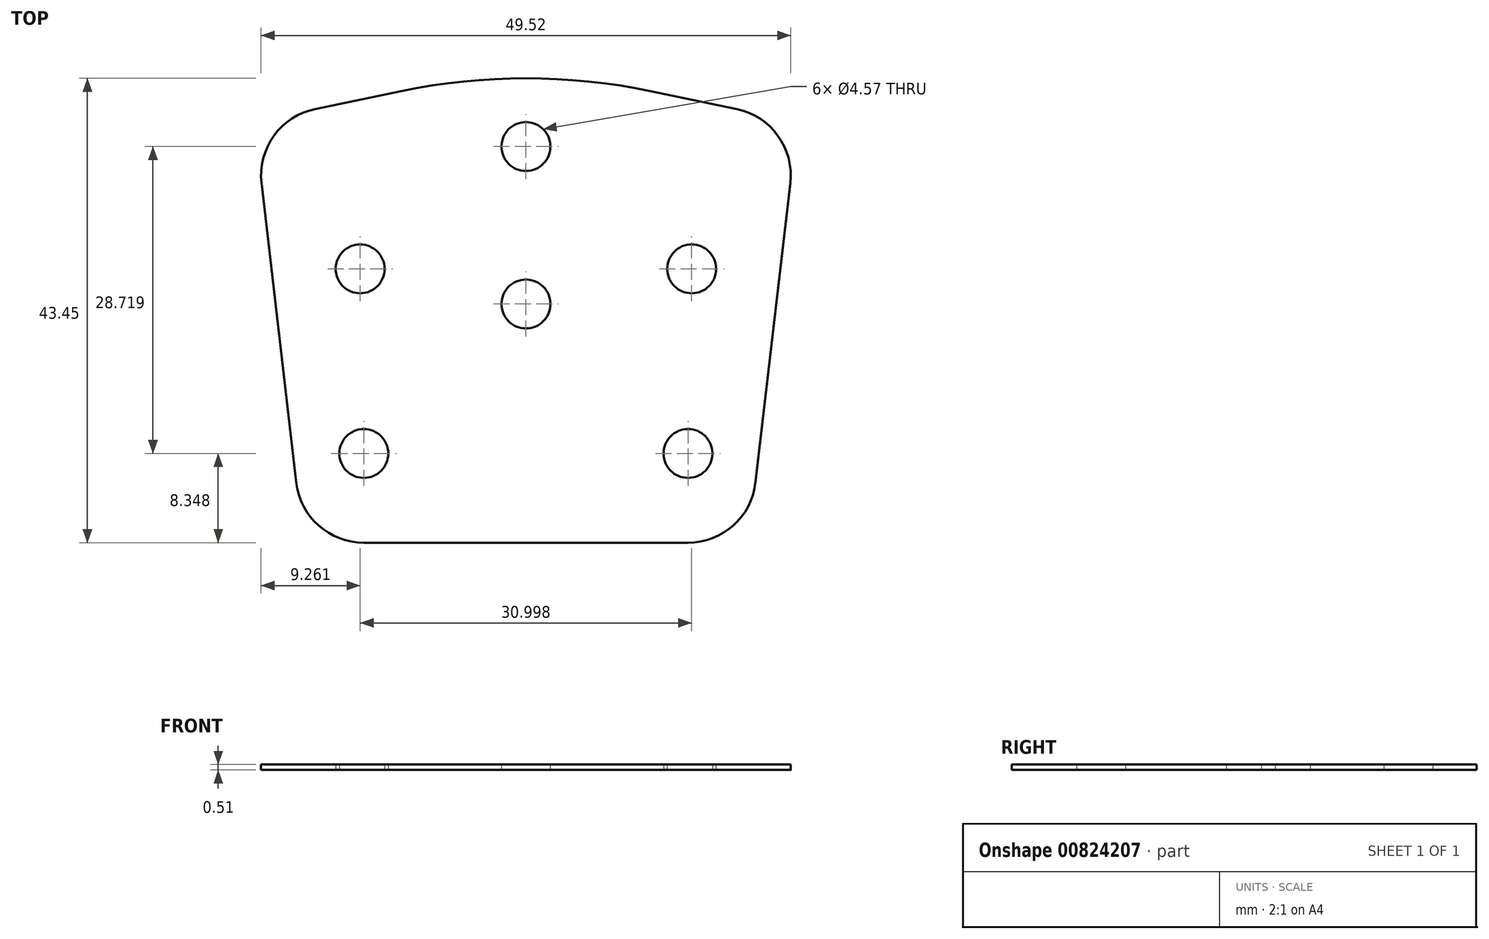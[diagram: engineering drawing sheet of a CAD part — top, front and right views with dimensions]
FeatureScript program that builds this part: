
annotation { "Feature Type Name" : "Feature", "Feature Type Description" : "" }
export const myFeature = defineFeature(function(context is Context, id is Id, definition is map)
    precondition{}
    {
        {
            var Q0;
            Q0=qCreatedBy(makeId("Top.planeOp"),FACE);
            var sketch = newSketch(context, id + "F0", { "sketchPlane" : qUnion([Q0])});
            skLineSegment(sketch, "E0", {"start": v(0, 0) * mm, "end": v(15.16, 0) * mm});
            skLineSegment(sketch, "E1", {"start": v(21.46, 5.62) * mm, "end": v(24.72, 33.62) * mm});
            skLineSegment(sketch, "E2", {"start": v(19.7, 40.57) * mm, "end": v(11.63, 42.25) * mm});
            skPoint(sketch, "E3.visualSharp", {"position": v(25.4, 39.4) * mm});
            skArc(sketch, "E3.filletArc", {"start": v(24.72, 33.62) * mm, "mid": v(23.56, 38.07) * mm, "end": v(19.7, 40.57) * mm});
            skPoint(sketch, "E4.visualSharp", {"position": v(20.81, 0) * mm});
            skArc(sketch, "E4.filletArc", {"start": v(15.16, 0) * mm, "mid": v(19.38, 1.6) * mm, "end": v(21.46, 5.62) * mm});
            skLineSegment(sketch, "E5", {"start": v(0, 44.67) * mm, "end": v(0, 0) * mm, "construction": true});
            skLineSegment(sketch, "E6.MirrorCS", {"start": v(-21.46, 5.62) * mm, "end": v(-24.72, 33.62) * mm});
            skLineSegment(sketch, "E7.MirrorCS", {"start": v(-19.7, 40.57) * mm, "end": v(-11.63, 42.25) * mm});
            skPoint(sketch, "E8.MirrorP", {"position": v(-25.4, 39.4) * mm});
            skPoint(sketch, "E9.MirrorP", {"position": v(-20.81, 0) * mm});
            skArc(sketch, "E10.MirrorCS", {"start": v(-15.16, 0) * mm, "mid": v(-19.38, 1.6) * mm, "end": v(-21.46, 5.62) * mm});
            skLineSegment(sketch, "E11.MirrorCS", {"start": v(0, 0) * mm, "end": v(-15.16, 0) * mm});
            skArc(sketch, "E12.MirrorCS", {"start": v(-24.72, 33.62) * mm, "mid": v(-23.56, 38.07) * mm, "end": v(-19.7, 40.57) * mm});
            skPoint(sketch, "E13.visualSharp", {"position": v(0, 44.67) * mm});
            skArc(sketch, "E13.filletArc", {"start": v(11.63, 42.25) * mm, "mid": v(0, 43.45) * mm, "end": v(-11.63, 42.25) * mm});
            skCircle(sketch, "E14", {"center": v(15.5, 25.62) * mm, "radius": 2.29 * mm});
            skCircle(sketch, "E15", {"center": v(15.16, 8.35) * mm, "radius": 2.29 * mm});
            skCircle(sketch, "E16", {"center": v(0, 22.33) * mm, "radius": 2.29 * mm});
            skCircle(sketch, "E17.MirrorC", {"center": v(-15.5, 25.62) * mm, "radius": 2.29 * mm});
            skCircle(sketch, "E18.MirrorC", {"center": v(-15.16, 8.35) * mm, "radius": 2.29 * mm});
            skCircle(sketch, "E19", {"center": v(0, 37.07) * mm, "radius": 2.29 * mm});
            skSolve(sketch);
        }
        {
            var Q0;
            Q0=makeQuery(id+"F0.imprint","IMPRINT",FACE,{"disambiguationData":[TD([[makeQuery(id+"F0.imprint","IMPRINT",EDGE,{"derivedFrom":sQuery(id+"F0.wireOp",EDGE,"E0")}),1.0]])]});
            extrude(context, id + "F1", {"entities" : qUnion([Q0]), "depth" : 0.5 * mm, "offsetDistance" : 25.4 * mm});
        }
    });
